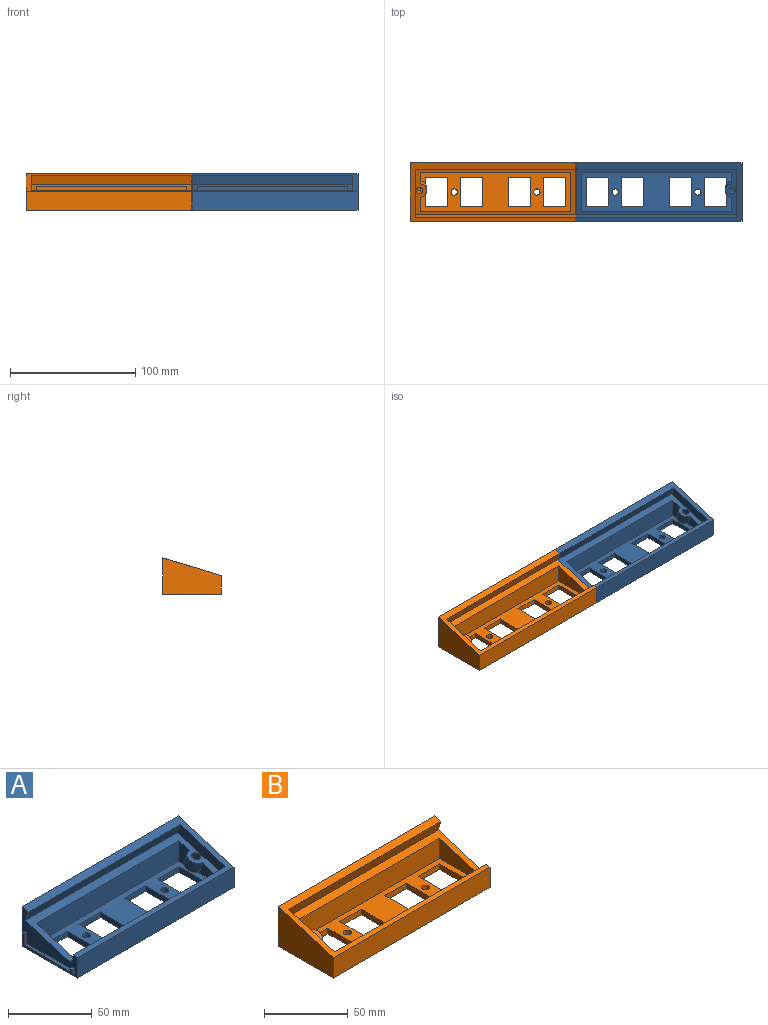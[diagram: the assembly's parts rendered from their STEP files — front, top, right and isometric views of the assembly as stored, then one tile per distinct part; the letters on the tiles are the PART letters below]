
ASSEMBLY  parts=2 mates=1
PART A: 46 faces, bbox 134.4x46.5x29 mm
  f0: plane 46.5x29mm, normal (-1,0,0), area 613.5mm2, adj f1,f3,f4,f26,f30,f31,f32,f37
  f1: plane 128.4x38.5mm, normal (0,-0.29,0.96), area 1351.7mm2, adj f0,f2,f6,f27,f28,f29,f31,f32
  f2: plane 30.5x14.78mm, normal (-1,0,0), area 216.8mm2, adj f1,f25,f27,f29,f34,f35,f36
  f3: plane 132.4x46.5mm, normal (0,-0.29,0.96), area 1268.6mm2, adj f0,f4,f5,f6,f30,f31,f32
  f4: plane 132.4x14.78mm, normal (0,-1,0), area 1957.3mm2, adj f0,f3,f5,f26
  f5: plane 46.5x29mm, normal (1,0,0), area 1018mm2, adj f3,f4,f26,f30
  f6: plane 40.67x18.88mm, normal (-1,0,0), area 299.4mm2, adj f1,f3,f31,f32
  f7: plane 22.5x4mm, normal (1,0,0), area 90mm2, adj f8,f21,f25,f26
  f8: plane 18.1x4mm, normal (0,-1,0), area 72.4mm2, adj f7,f9,f25,f26
  f9: plane 22.5x4mm, normal (-1,0,0), area 90mm2, adj f8,f21,f25,f26
  f10: plane 22.5x4mm, normal (1,0,0), area 90mm2, adj f11,f22,f25,f26
  f11: plane 18.1x4mm, normal (0,-1,0), area 72.4mm2, adj f10,f12,f25,f26
  f12: plane 22.5x4mm, normal (-1,0,0), area 90mm2, adj f11,f22,f25,f26
  f13: plane 22.5x4mm, normal (1,0,0), area 90mm2, adj f14,f23,f25,f26
  f14: plane 18.1x4mm, normal (0,-1,0), area 72.4mm2, adj f13,f15,f25,f26
  f15: plane 22.5x4mm, normal (-1,0,0), area 90mm2, adj f14,f23,f25,f26
  f16: plane 22.5x4mm, normal (1,0,0), area 90mm2, adj f17,f24,f25,f26
  f17: plane 18.1x4mm, normal (0,-1,0), area 72.4mm2, adj f16,f18,f25,f26
  f18: plane 22.5x4mm, normal (-1,0,0), area 90mm2, adj f17,f24,f25,f26
  f19: cylinder r=2.5mm len=5mm, axis (0,0,-1), area 62.8mm2, adj f25,f26
  f20: cylinder r=2.5mm len=5mm, axis (0,0,-1), area 62.8mm2, adj f25,f26
  f21: plane 18.1x4mm, normal (0,1,0), area 72.4mm2, adj f7,f9,f25,f26
  f22: plane 18.1x4mm, normal (0,1,0), area 72.4mm2, adj f10,f12,f25,f26
  f23: plane 18.1x4mm, normal (0,1,0), area 72.4mm2, adj f13,f15,f25,f26
  f24: plane 18.1x4mm, normal (0,1,0), area 72.4mm2, adj f16,f18,f25,f26
  f25: plane 120.4x30.5mm, normal (0,0,1), area 2003.9mm2, adj f2,f7,f8,f9,f10,f11,f12,f13
  f26: plane 132.4x46.5mm, normal (0,0,-1), area 4488.3mm2, adj f0,f4,f5,f7,f8,f9,f10,f11
  f27: plane 120.4x14.78mm, normal (0,-1,0), area 1779.2mm2, adj f1,f2,f25,f28
  f28: plane 30.5x14.78mm, normal (1,0,0), area 308.5mm2, adj f1,f25,f27,f29
  f29: plane 120.4x5.45mm, normal (0,1,0), area 656.5mm2, adj f1,f2,f25,f28
  f30: plane 132.4x29mm, normal (0,1,0), area 3839.6mm2, adj f0,f3,f5,f26
  f31: plane 128.4x7.11mm, normal (0,0.96,0.29), area 954.9mm2, adj f0,f1,f3,f6
  f32: plane 128.4x7.11mm, normal (0,-0.96,-0.29), area 954.9mm2, adj f0,f1,f3,f6
  f33: cylinder r=2.75mm len=9.26mm, axis (0,-0.29,0.96), area 138.2mm2, adj f1,f35,f36
  f34: cylinder r=5.75mm len=13.3mm, axis (0,-0.29,0.96), area 136.5mm2, adj f1,f2,f35
  f35: plane 10.96x5.25mm, normal (0,0.29,-0.96), area 37mm2, adj f2,f33,f34
  f36: plane 5.26x3.25mm, normal (0,-0.29,0.96), area 14.6mm2, adj f2,f33
  f37: plane 2x2mm, normal (0,0,1), area 4mm2, adj f0,f38,f44,f45
  f38: plane 10x2mm, normal (0,1,0), area 20mm2, adj f0,f37,f39,f45
  f39: plane 42.5x2mm, normal (0,0,-1), area 85mm2, adj f0,f38,f40,f45
  f40: plane 4x2mm, normal (0,-1,0), area 8mm2, adj f0,f39,f41,f45
  f41: plane 2x2mm, normal (0,0,1), area 4mm2, adj f0,f40,f42,f45
  f42: plane 2x2mm, normal (0,1,0), area 4mm2, adj f0,f41,f43,f45
  f43: plane 38.5x2mm, normal (0,0,1), area 77mm2, adj f0,f42,f44,f45
  f44: plane 8x2mm, normal (0,-1,0), area 16mm2, adj f0,f37,f43,f45
  f45: plane 42.5x10mm, normal (-1,0,0), area 105mm2, adj f37,f38,f39,f40,f41,f42,f43,f44
PART B: 46 faces, bbox 132.4x46.5x29 mm
  f0: plane 128.4x38.5mm, normal (0,-0.29,0.96), area 1351.7mm2, adj f1,f24,f25,f26,f27,f28,f31,f32
  f1: plane 46.5x29mm, normal (1,0,0), area 613.5mm2, adj f0,f2,f23,f29,f30,f31,f32,f37
  f2: plane 132.4x46.5mm, normal (0,-0.29,0.96), area 1268.6mm2, adj f1,f3,f28,f29,f30,f31,f32
  f3: plane 46.5x29mm, normal (-1,0,0), area 1018mm2, adj f2,f23,f29,f30
  f4: plane 22.5x4mm, normal (1,0,0), area 90mm2, adj f5,f18,f22,f23
  f5: plane 18.1x4mm, normal (0,-1,0), area 72.4mm2, adj f4,f6,f22,f23
  f6: plane 22.5x4mm, normal (-1,0,0), area 90mm2, adj f5,f18,f22,f23
  f7: plane 22.5x4mm, normal (1,0,0), area 90mm2, adj f8,f19,f22,f23
  f8: plane 18.1x4mm, normal (0,-1,0), area 72.4mm2, adj f7,f9,f22,f23
  f9: plane 22.5x4mm, normal (-1,0,0), area 90mm2, adj f8,f19,f22,f23
  f10: plane 22.5x4mm, normal (1,0,0), area 90mm2, adj f11,f20,f22,f23
  f11: plane 18.1x4mm, normal (0,-1,0), area 72.4mm2, adj f10,f12,f22,f23
  f12: plane 22.5x4mm, normal (-1,0,0), area 90mm2, adj f11,f20,f22,f23
  f13: plane 22.5x4mm, normal (1,0,0), area 90mm2, adj f14,f21,f22,f23
  f14: plane 18.1x4mm, normal (0,-1,0), area 72.4mm2, adj f13,f15,f22,f23
  f15: plane 22.5x4mm, normal (-1,0,0), area 90mm2, adj f14,f21,f22,f23
  f16: cylinder r=2.5mm len=5mm, axis (0,0,-1), area 62.8mm2, adj f22,f23
  f17: cylinder r=2.5mm len=5mm, axis (0,0,-1), area 62.8mm2, adj f22,f23
  f18: plane 18.1x4mm, normal (0,1,0), area 72.4mm2, adj f4,f6,f22,f23
  f19: plane 18.1x4mm, normal (0,1,0), area 72.4mm2, adj f7,f9,f22,f23
  f20: plane 18.1x4mm, normal (0,1,0), area 72.4mm2, adj f10,f12,f22,f23
  f21: plane 18.1x4mm, normal (0,1,0), area 72.4mm2, adj f13,f15,f22,f23
  f22: plane 120.4x30.5mm, normal (0,0,1), area 2003.9mm2, adj f4,f5,f6,f7,f8,f9,f10,f11
  f23: plane 132.4x46.5mm, normal (0,0,-1), area 4488.3mm2, adj f1,f3,f4,f5,f6,f7,f8,f9
  f24: plane 120.4x14.78mm, normal (0,-1,0), area 1779.2mm2, adj f0,f22,f25,f27
  f25: plane 30.5x14.78mm, normal (1,0,0), area 216.8mm2, adj f0,f22,f24,f26,f34,f35,f36
  f26: plane 120.4x5.45mm, normal (0,1,0), area 656.5mm2, adj f0,f22,f25,f27
  f27: plane 30.5x14.78mm, normal (-1,0,0), area 308.5mm2, adj f0,f22,f24,f26
  f28: plane 40.67x18.88mm, normal (1,0,0), area 299.4mm2, adj f0,f2,f31,f32
  f29: plane 132.4x29mm, normal (0,1,0), area 3839.6mm2, adj f1,f2,f3,f23
  f30: plane 132.4x14.78mm, normal (0,-1,0), area 1957.3mm2, adj f1,f2,f3,f23
  f31: plane 128.4x7.11mm, normal (0,0.96,0.29), area 954.9mm2, adj f0,f1,f2,f28
  f32: plane 128.4x7.11mm, normal (0,-0.96,-0.29), area 954.9mm2, adj f0,f1,f2,f28
  f33: cylinder r=2.75mm len=9.26mm, axis (0,-0.29,0.96), area 138.2mm2, adj f0,f35,f36
  f34: cylinder r=5.75mm len=13.3mm, axis (0,-0.29,0.96), area 136.5mm2, adj f0,f25,f35
  f35: plane 10.96x5.25mm, normal (0,0.29,-0.96), area 37mm2, adj f25,f33,f34
  f36: plane 5.26x3.25mm, normal (0,-0.29,0.96), area 14.6mm2, adj f25,f33
  f37: plane 2x2mm, normal (0,0,-1), area 4mm2, adj f1,f38,f44,f45
  f38: plane 4x2mm, normal (0,1,0), area 8mm2, adj f1,f37,f39,f45
  f39: plane 42.5x2mm, normal (0,0,1), area 85mm2, adj f1,f38,f40,f45
  f40: plane 10x2mm, normal (0,-1,0), area 20mm2, adj f1,f39,f41,f45
  f41: plane 2x2mm, normal (0,0,-1), area 4mm2, adj f1,f40,f42,f45
  f42: plane 8x2mm, normal (0,1,0), area 16mm2, adj f1,f41,f43,f45
  f43: plane 38.5x2mm, normal (0,0,-1), area 77mm2, adj f1,f42,f44,f45
  f44: plane 2x2mm, normal (0,-1,0), area 4mm2, adj f1,f37,f43,f45
  f45: plane 42.5x10mm, normal (1,0,0), area 105mm2, adj f37,f38,f39,f40,f41,f42,f43,f44
PLACE A t=(70.76,-14.35,15.39)mm
PLACE B t=(-57.36,-14.35,15.39)mm
MATE fastened A.f45 <-> B.f45  axis (-1,0,0) through (4.84,5.9,27.39)mm
